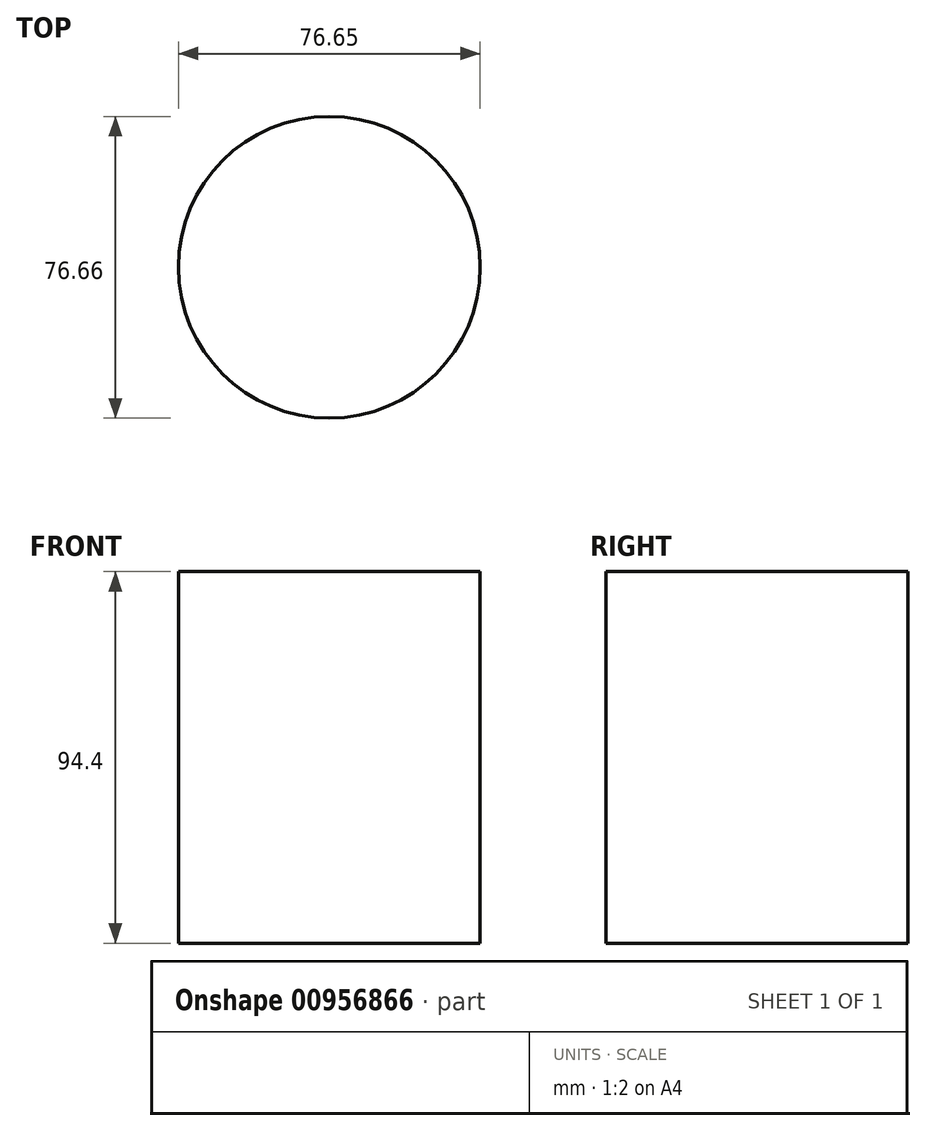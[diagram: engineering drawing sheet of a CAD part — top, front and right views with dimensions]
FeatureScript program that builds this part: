
annotation { "Feature Type Name" : "Feature", "Feature Type Description" : "" }
export const myFeature = defineFeature(function(context is Context, id is Id, definition is map)
    precondition{}
    {
        {
            var Q0;
            Q0=qCreatedBy(makeId("Top.planeOp"),FACE);
            var sketch = newSketch(context, id + "F0", { "sketchPlane" : qUnion([Q0])});
            skCircle(sketch, "E0", {"center": v(36.1, 0) * mm, "radius": 38.33 * mm});
            skSolve(sketch);
        }
        {
            var Q0;
            Q0=makeQuery(id+"F0.imprint","IMPRINT",FACE,{"disambiguationData":[TD([[makeQuery(id+"F0.imprint","IMPRINT",EDGE,{"derivedFrom":sQuery(id+"F0.wireOp",EDGE,"E0")}),1.0]])]});
            extrude(context, id + "F1", {"entities" : qUnion([Q0]), "depth" : 94.4 * mm, "offsetDistance" : 25.4 * mm});
        }
    });
